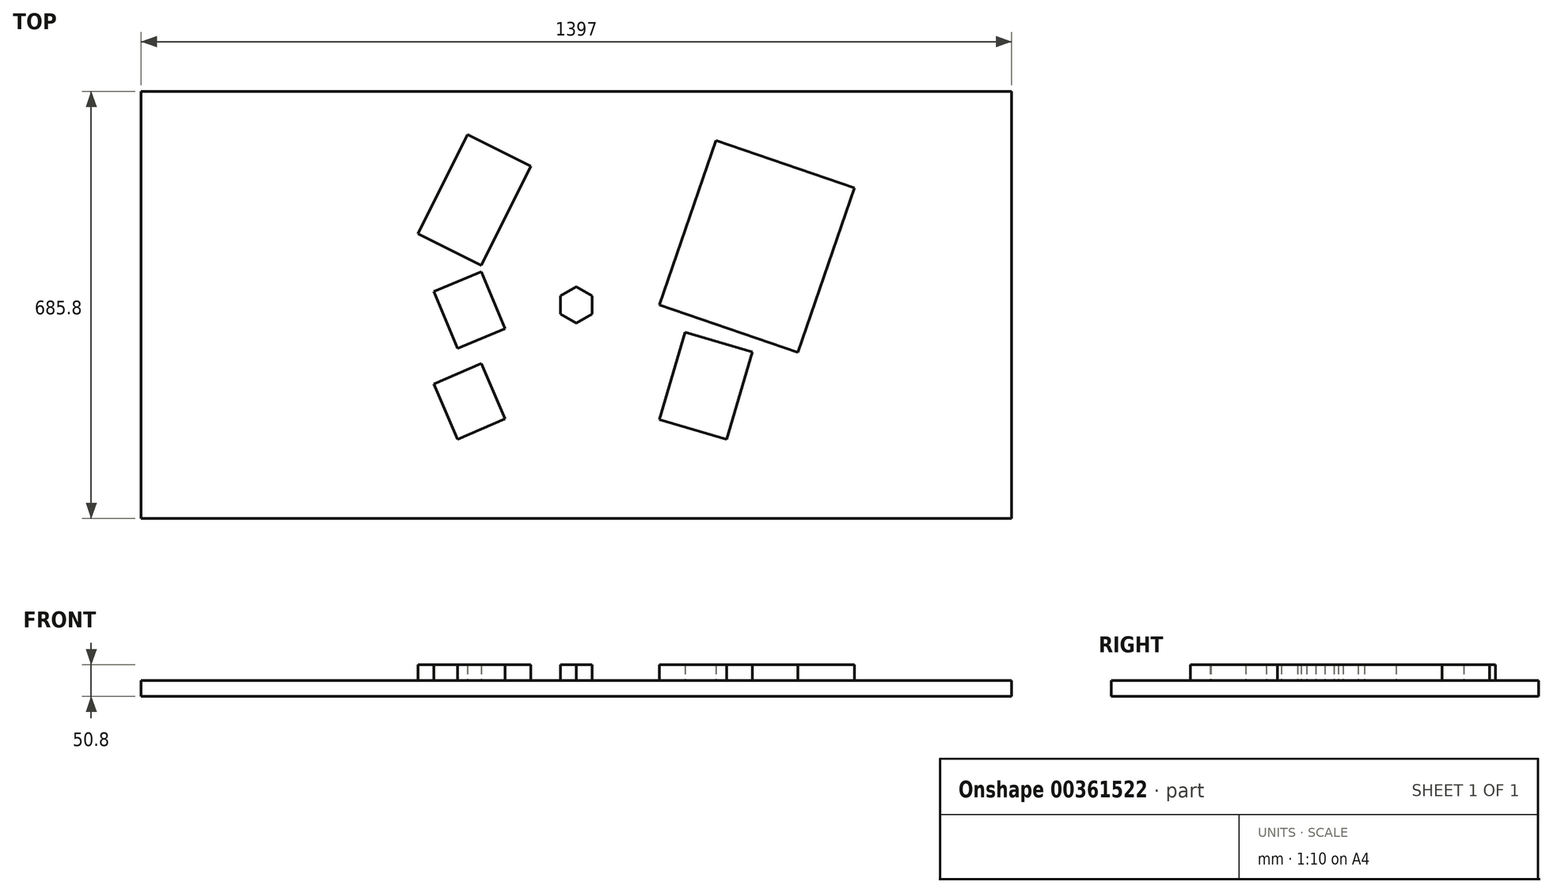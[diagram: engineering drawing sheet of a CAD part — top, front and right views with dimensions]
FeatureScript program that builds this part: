
annotation { "Feature Type Name" : "Feature", "Feature Type Description" : "" }
export const myFeature = defineFeature(function(context is Context, id is Id, definition is map)
    precondition{}
    {
        {
            var Q0;
            Q0=qCreatedBy(makeId("Top.planeOp"),FACE);
            var sketch = newSketch(context, id + "F0", { "sketchPlane" : qUnion([Q0])});
            skLineSegment(sketch, "E0.bottom", {"start": v(698.5, 342.9) * mm, "end": v(-698.5, 342.9) * mm});
            skLineSegment(sketch, "E0.top", {"start": v(698.5, -342.9) * mm, "end": v(-698.5, -342.9) * mm});
            skLineSegment(sketch, "E0.left", {"start": v(698.5, 342.9) * mm, "end": v(698.5, -342.9) * mm});
            skLineSegment(sketch, "E0.right", {"start": v(-698.5, 342.9) * mm, "end": v(-698.5, -342.9) * mm});
            skPoint(sketch, "E0.middle", {"position": v(0, 0) * mm});
            skSolve(sketch);
        }
        {
            var Q0;
            Q0 = qSketchRegion(id + "F0", true);
            extrude(context, id + "F1", {"entities" : qUnion([Q0]), "depth" : 25.4 * mm});
        }
        {
            var Q0;
            Q0=makeQuery(id+"F1.opExtrude","CAP_FACE",FACE,{"disambiguationData":[OSD([sQuery(id+"F0.wireOp",EDGE,"E0.bottom"),sQuery(id+"F0.wireOp",EDGE,"E0.top"),sQuery(id+"F0.wireOp",EDGE,"E0.left"),sQuery(id+"F0.wireOp",EDGE,"E0.right")])],"isStart":false});
            var sketch = newSketch(context, id + "F2", { "sketchPlane" : qUnion([Q0])});
            skLineSegment(sketch, "E1.bottom", {"start": v(101.6, -215.9) * mm, "end": v(-101.6, -215.9) * mm, "construction": true});
            skLineSegment(sketch, "E1.top", {"start": v(101.6, 139.7) * mm, "end": v(-101.6, 139.7) * mm, "construction": true});
            skLineSegment(sketch, "E1.left", {"start": v(101.6, -215.9) * mm, "end": v(101.6, 139.7) * mm, "construction": true});
            skLineSegment(sketch, "E1.right", {"start": v(-101.6, -215.9) * mm, "end": v(-101.6, 139.7) * mm, "construction": true});
            skPoint(sketch, "E1.middle", {"position": v(0, -38.1) * mm});
            skCircle(sketch, "E2.cCircle", {"center": v(0, 0) * mm, "radius": 25.4 * mm, "construction": true});
            skLineSegment(sketch, "E2.0", {"start": v(25.4, 14.66) * mm, "end": v(25.4, -14.66) * mm});
            skLineSegment(sketch, "E2.1", {"start": v(25.4, -14.66) * mm, "end": v(0, -29.33) * mm});
            skLineSegment(sketch, "E2.2", {"start": v(0, -29.33) * mm, "end": v(-25.4, -14.66) * mm});
            skLineSegment(sketch, "E2.3", {"start": v(-25.4, -14.66) * mm, "end": v(-25.4, 14.66) * mm});
            skLineSegment(sketch, "E2.4", {"start": v(-25.4, 14.66) * mm, "end": v(0, 29.33) * mm});
            skLineSegment(sketch, "E2.5", {"start": v(0, 29.33) * mm, "end": v(25.4, 14.66) * mm});
            skPoint(sketch, "E2.0.midPoint", {"position": v(25.4, 0) * mm});
            skLineSegment(sketch, "E3.bottom", {"start": v(-114.3, -183.24) * mm, "end": v(-190.5, -215.9) * mm});
            skLineSegment(sketch, "E3.top", {"start": v(-152.4, -94.34) * mm, "end": v(-228.6, -127) * mm});
            skLineSegment(sketch, "E3.left", {"start": v(-114.3, -183.24) * mm, "end": v(-152.4, -94.34) * mm});
            skLineSegment(sketch, "E3.right", {"start": v(-190.5, -215.9) * mm, "end": v(-228.6, -127) * mm});
            skPoint(sketch, "E3.middle", {"position": v(-171.45, -155.12) * mm});
            skLineSegment(sketch, "E4.bottom", {"start": v(-114.3, -38.1) * mm, "end": v(-190.5, -69.85) * mm});
            skLineSegment(sketch, "E4.top", {"start": v(-152.4, 53.34) * mm, "end": v(-228.6, 21.59) * mm});
            skLineSegment(sketch, "E4.left", {"start": v(-114.3, -38.1) * mm, "end": v(-152.4, 53.34) * mm});
            skLineSegment(sketch, "E4.right", {"start": v(-190.5, -69.85) * mm, "end": v(-228.6, 21.59) * mm});
            skPoint(sketch, "E4.middle", {"position": v(-171.45, -8.26) * mm});
            skLineSegment(sketch, "E5.bottom", {"start": v(-152.4, 63.5) * mm, "end": v(-254, 114.3) * mm});
            skLineSegment(sketch, "E5.top", {"start": v(-72.89, 222.53) * mm, "end": v(-174.49, 273.33) * mm});
            skLineSegment(sketch, "E5.left", {"start": v(-152.4, 63.5) * mm, "end": v(-72.89, 222.53) * mm});
            skLineSegment(sketch, "E5.right", {"start": v(-254, 114.3) * mm, "end": v(-174.49, 273.33) * mm});
            skPoint(sketch, "E5.middle", {"position": v(-163.44, 168.41) * mm});
            skLineSegment(sketch, "E6.bottom", {"start": v(355.6, -76.2) * mm, "end": v(133.35, 0) * mm});
            skLineSegment(sketch, "E6.top", {"start": v(446.22, 188.1) * mm, "end": v(223.97, 264.3) * mm});
            skLineSegment(sketch, "E6.left", {"start": v(355.6, -76.2) * mm, "end": v(446.22, 188.1) * mm});
            skLineSegment(sketch, "E6.right", {"start": v(133.35, 0) * mm, "end": v(223.97, 264.3) * mm});
            skLineSegment(sketch, "E7.bottom", {"start": v(241.3, -215.9) * mm, "end": v(133.35, -184.15) * mm});
            skLineSegment(sketch, "E7.top", {"start": v(282.5, -75.83) * mm, "end": v(174.55, -44.08) * mm});
            skLineSegment(sketch, "E7.left", {"start": v(241.3, -215.9) * mm, "end": v(282.5, -75.83) * mm});
            skLineSegment(sketch, "E7.right", {"start": v(133.35, -184.15) * mm, "end": v(174.55, -44.08) * mm});
            skPoint(sketch, "E7.middle", {"position": v(207.92, -129.99) * mm});
            skPoint(sketch, "E8", {"position": v(279.32, 105.13) * mm});
            skSolve(sketch);
        }
        {
            var Q0;
            Q0 = qSketchRegion(id + "F2", true);
            extrude(context, id + "F3", {"entities" : qUnion([Q0]), "depth" : 25.4 * mm});
        }
    });
